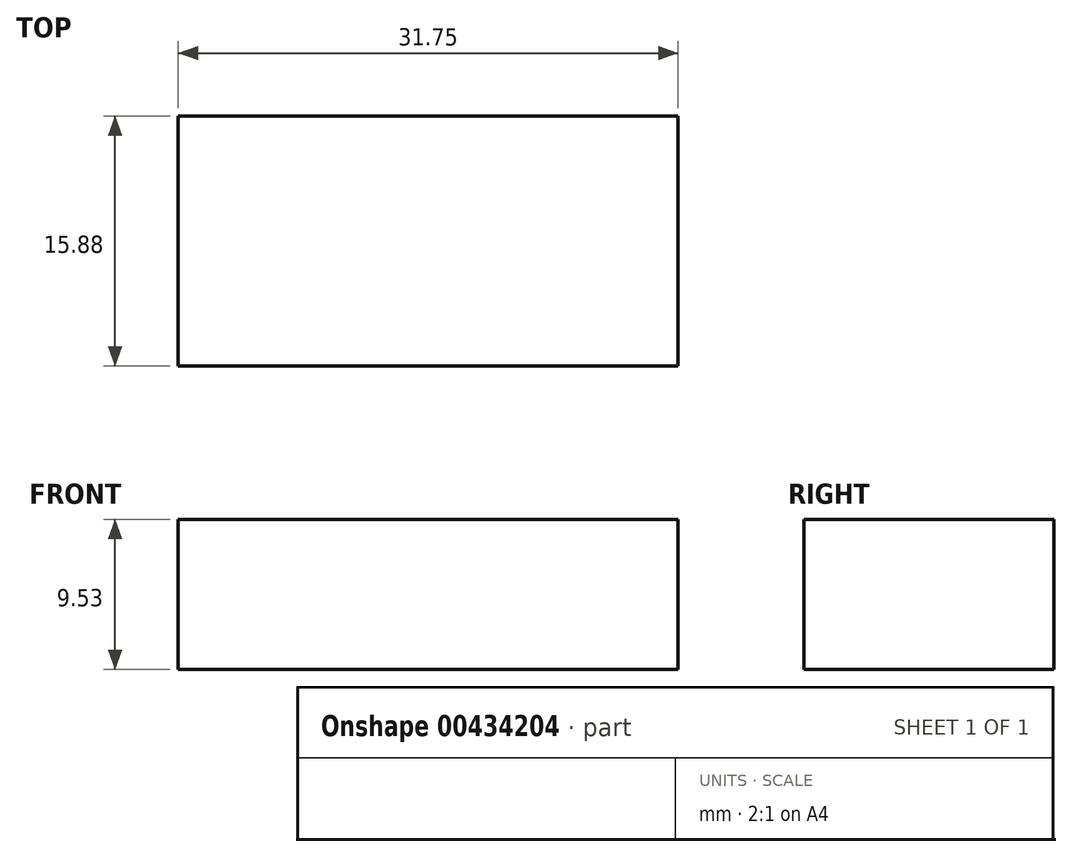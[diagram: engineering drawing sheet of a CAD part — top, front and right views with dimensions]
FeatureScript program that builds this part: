
annotation { "Feature Type Name" : "Feature", "Feature Type Description" : "" }
export const myFeature = defineFeature(function(context is Context, id is Id, definition is map)
    precondition{}
    {
        {
            var Q0;
            Q0=qCreatedBy(makeId("Top.planeOp"),FACE);
            var sketch = newSketch(context, id + "F0", { "sketchPlane" : qUnion([Q0])});
            skLineSegment(sketch, "E0.bottom", {"start": v(-44.68, -7.07) * mm, "end": v(-12.93, -7.07) * mm});
            skLineSegment(sketch, "E0.top", {"start": v(-44.68, -22.95) * mm, "end": v(-12.93, -22.95) * mm});
            skLineSegment(sketch, "E0.left", {"start": v(-44.68, -7.07) * mm, "end": v(-44.68, -22.95) * mm});
            skLineSegment(sketch, "E0.right", {"start": v(-12.93, -7.07) * mm, "end": v(-12.93, -22.95) * mm});
            skSolve(sketch);
        }
        {
            var Q0;
            Q0 = qSketchRegion(id + "F0", true);
            extrude(context, id + "F1", {"entities" : qUnion([Q0]), "depth" : 9.52 * mm});
        }
    });
